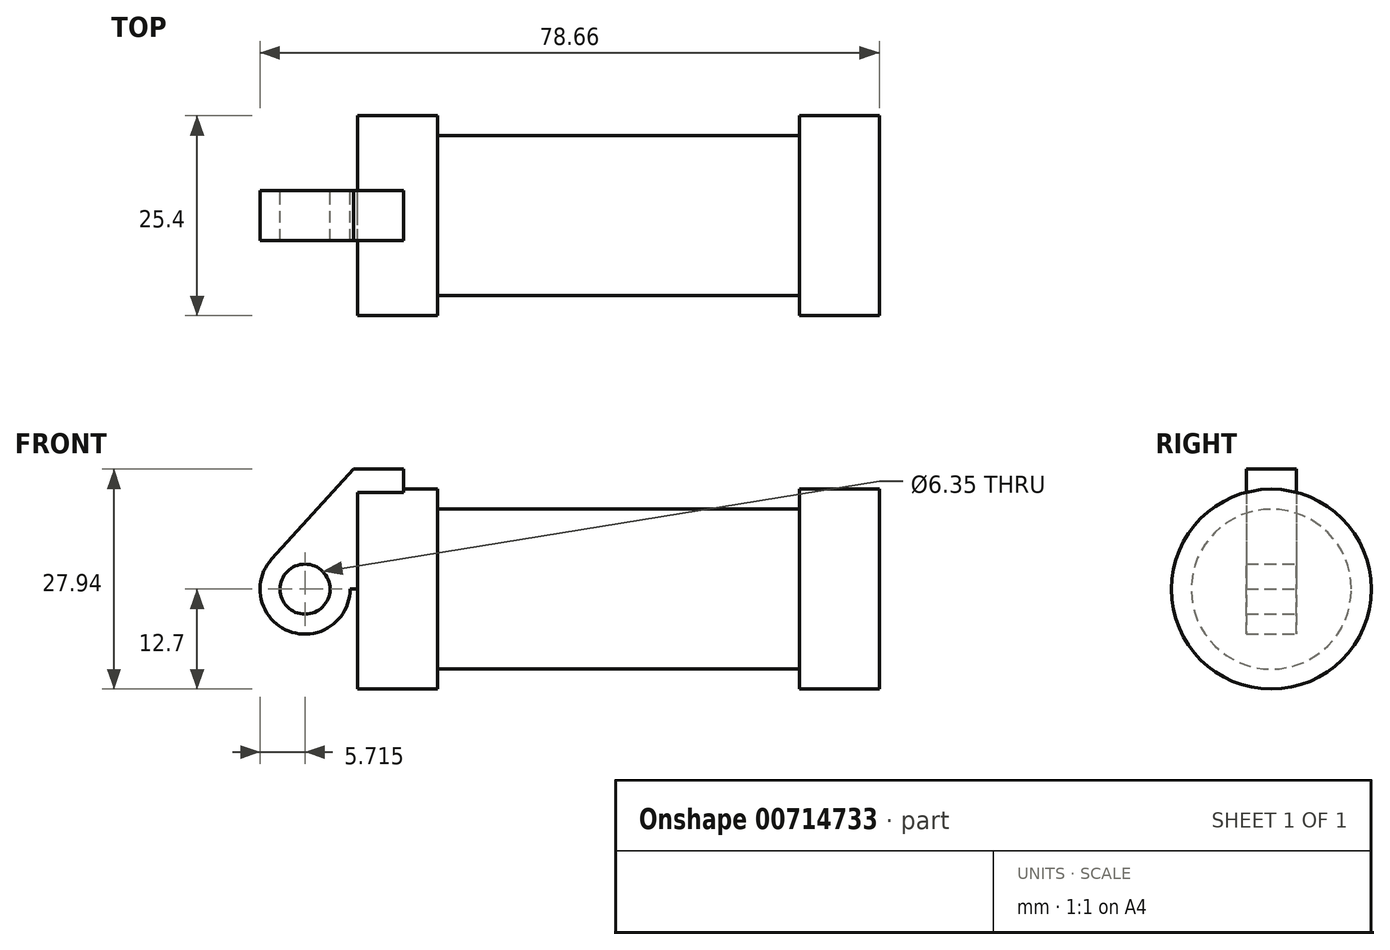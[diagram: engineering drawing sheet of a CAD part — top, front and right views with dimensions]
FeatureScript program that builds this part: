
annotation { "Feature Type Name" : "Feature", "Feature Type Description" : "" }
export const myFeature = defineFeature(function(context is Context, id is Id, definition is map)
    precondition{}
    {
        {
            var Q0;
            Q0=qCreatedBy(makeId("Front.planeOp"),FACE);
            var sketch = newSketch(context, id + "F0", { "sketchPlane" : qUnion([Q0])});
            skLineSegment(sketch, "E0", {"start": v(0, 0) * mm, "end": v(0, 12.7) * mm});
            skLineSegment(sketch, "E1", {"start": v(0, 12.7) * mm, "end": v(10.16, 12.7) * mm});
            skLineSegment(sketch, "E2", {"start": v(10.16, 12.7) * mm, "end": v(10.16, 10.16) * mm});
            skLineSegment(sketch, "E3", {"start": v(10.16, 10.16) * mm, "end": v(56.13, 10.16) * mm});
            skLineSegment(sketch, "E4", {"start": v(56.13, 10.16) * mm, "end": v(56.13, 12.7) * mm});
            skLineSegment(sketch, "E5", {"start": v(56.13, 12.7) * mm, "end": v(66.3, 12.7) * mm});
            skLineSegment(sketch, "E6", {"start": v(66.3, 12.7) * mm, "end": v(66.3, 0) * mm});
            skLineSegment(sketch, "E7", {"start": v(66.3, 0) * mm, "end": v(0, 0) * mm});
            skLineSegment(sketch, "E8", {"start": v(5.84, 15.24) * mm, "end": v(-0.5, 15.24) * mm});
            skLineSegment(sketch, "E9", {"start": v(-0.5, 15.24) * mm, "end": v(-10.88, 3.85) * mm});
            skLineSegment(sketch, "E10", {"start": v(0, 0) * mm, "end": v(-6.65, 0) * mm});
            skCircle(sketch, "E11", {"center": v(-6.65, 0) * mm, "radius": 5.72 * mm});
            skCircle(sketch, "E12", {"center": v(-6.65, 0) * mm, "radius": 3.18 * mm});
            skLineSegment(sketch, "E13", {"start": v(5.84, 15.24) * mm, "end": v(5.84, -9.4) * mm});
            skLineSegment(sketch, "E14", {"start": v(5.84, -9.4) * mm, "end": v(-8.18, -5.5) * mm});
            skLineSegment(sketch, "E15", {"start": v(0, 0) * mm, "end": v(0, -7.78) * mm});
            skLineSegment(sketch, "E16", {"start": v(0, -7.78) * mm, "end": v(0, 0) * mm});
            skSolve(sketch);
        }
        {
            var Q0;
            {var subQ0=sQuery(id+"F0.wireOp",EDGE,"E0");Q0=makeQuery(id+"F0.imprint","IMPRINT",FACE,{"disambiguationData":[TD([[makeQuery(id+"F0.imprint","IMPRINT",EDGE,{"derivedFrom":subQ0}),-1.0]])]});}
            var Q1;
            {var subQ0=sQuery(id+"F0.wireOp",EDGE,"E2");Q1=makeQuery(id+"F0.imprint","IMPRINT",FACE,{"disambiguationData":[TD([[makeQuery(id+"F0.imprint","IMPRINT",EDGE,{"derivedFrom":subQ0}),-1.0]])]});}
            var Q2;
            Q2=sQuery(id+"F0.wireOp",EDGE,"E7");
            revolve(context, id + "F1", {"surfaceOperationType" : NewSurfaceOperationType.NEW, "entities" : qUnion([Q0, Q1]), "axis" : qUnion([Q2]), "revolveType" : RevolveType.FULL});
        }
        {
            var Q0;
            {var subQ1=sQuery(id+"F0.wireOp",EDGE,"E0");Q0=makeQuery(id+"F0.imprint","IMPRINT",FACE,{"disambiguationData":[TD([[makeQuery(id+"F0.imprint","IMPRINT",EDGE,{"derivedFrom":subQ1}),1.0]])]});}
            var Q1;
            {var subQ5=sQuery(id+"F0.wireOp",EDGE,"E12");Q1=makeQuery(id+"F0.imprint","IMPRINT",FACE,{"disambiguationData":[TD([[makeQuery(id+"F0.imprint","IMPRINT",EDGE,{"derivedFrom":subQ5}),-1.0]])]});}
            var Q2;
            {var subQ0=sQuery(id+"F0.wireOp",EDGE,"E16");Q2=makeQuery(id+"F0.imprint","IMPRINT",FACE,{"disambiguationData":[TD([[makeQuery(id+"F0.imprint","IMPRINT",EDGE,{"derivedFrom":subQ0}),1.0]])]});}
            var Q3;
            {var subQ0=sQuery(id+"F0.wireOp",EDGE,"E0");Q3=makeQuery(id+"F0.imprint","IMPRINT",FACE,{"disambiguationData":[TD([[makeQuery(id+"F0.imprint","IMPRINT",EDGE,{"derivedFrom":subQ0}),-1.0]])]});}
            var Q4;
            {var subQ0=sQuery(id+"F0.wireOp",EDGE,"E16");Q4=makeQuery(id+"F0.imprint","IMPRINT",FACE,{"disambiguationData":[TD([[makeQuery(id+"F0.imprint","IMPRINT",EDGE,{"derivedFrom":subQ0}),-1.0]])]});}
            extrude(context, id + "F2", {"entities" : qUnion([Q0, Q1, Q2, Q3, Q4]), "operationType" : NewBodyOperationType.ADD, "endBound" : BoundingType.SYMMETRIC, "depth" : 6.35 * mm, "offsetDistance" : 25.4 * mm});
        }
    });
